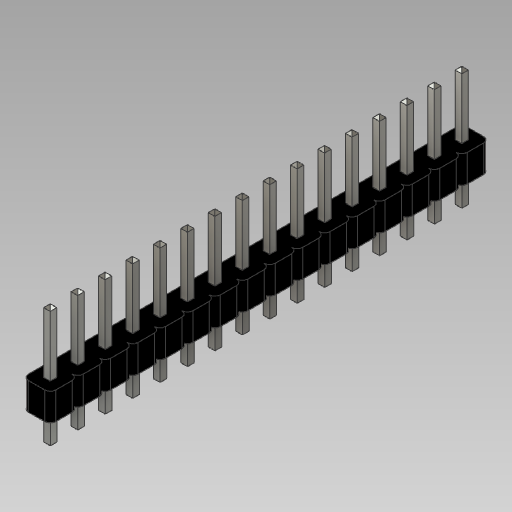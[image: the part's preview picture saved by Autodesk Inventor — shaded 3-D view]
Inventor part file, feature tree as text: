
AUTODESK INVENTOR PART (.ipt)
format: ipt  version: 2020 (Build 240168000, 168)  size: 726,528 bytes
history: native  units: in
note: dims shown in document units (in); Inventor stores cm internally (conversion verified against a paired STEP export)
features: other x4, extrude x3, sketch x3, chamfer x2
ambient origin geometry x8: Origin, YZ Plane, XZ Plane, XY Plane, X Axis, Y Axis, Z Axis, Center Point
bodies: Solid1 (feature_tree)
feature tree (12):
  extrude  "Extrusion1"  Depth=0.02in
  extrude  "Extrusion2"  Depth=0.1in TaperAngle=0.0deg
  chamfer  "Chamfer2"  Distance=0.1in
  extrude  "Extrusion3"  Depth=0.23in TaperAngle=0.0deg
  chamfer  "Chamfer4"  Distance=0.01in Angle=45.0deg
  other  "Work Point1"
  other  "Work Point2"
  other  "Work Axis1"
  other  "Work Axis2"
  sketch  "Sketch1"  dims[d0=0.1in d1=0.02in]
  sketch  "Sketch2"  dims[d2=6.2992in d4=0.1in d5=0.3937in d7=1.0in d9=0.1in d10=0.0in]
  sketch  "Sketch6"  dims[d11=0.024in d12=6.2992in d14=0.1in d15=0.3937in d17=1.0in d19=0.23in d20=0.0in d26=0.01in d27=0.125in d28=45.0deg d29=6.2992in d31=0.1in d32=0.3937in d34=1.0in d36=0.114in d37=0.0in d41=0.01in d42=0.125in d43=45.0deg]
